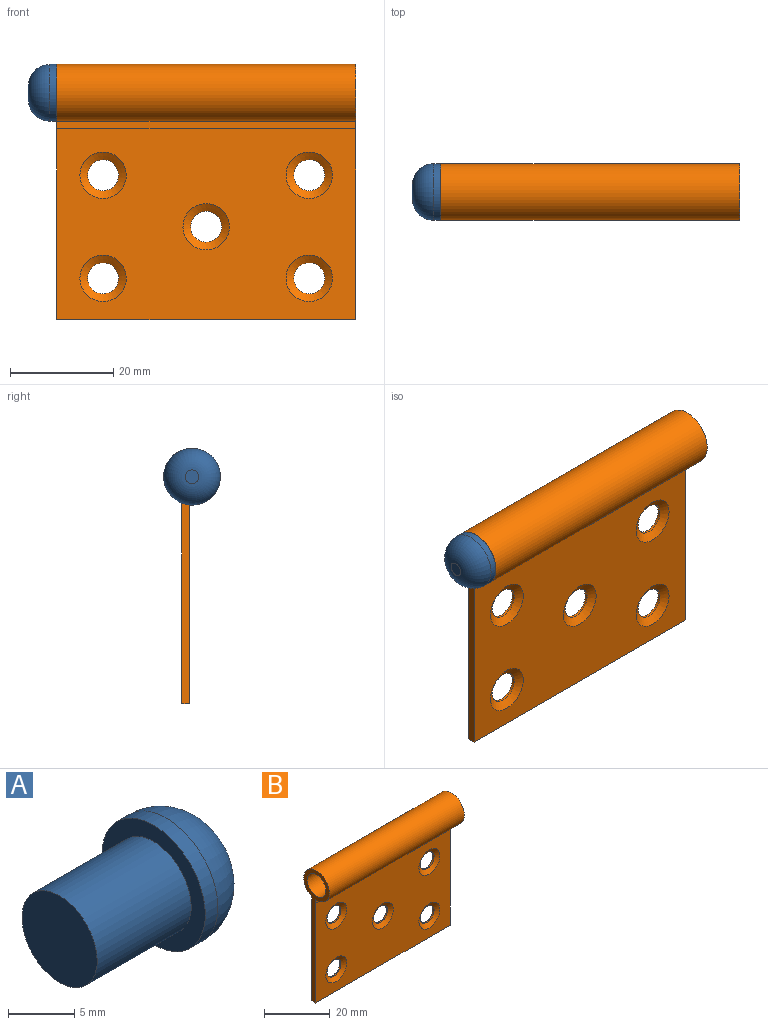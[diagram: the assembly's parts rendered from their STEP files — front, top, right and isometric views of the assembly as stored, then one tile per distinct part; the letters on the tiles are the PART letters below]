
ASSEMBLY  parts=2 mates=1
PART A: 6 faces, bbox 15.5x11x11 mm
  f0: cylinder r=5.5mm len=11mm, axis (-1,0,0), area 46.1mm2, adj f2,f5
  f1: plane 2.67x2.67mm, normal (1,0,0), area 5.6mm2, adj f5
  f2: plane 11x11mm, normal (-1,0,0), area 44.8mm2, adj f0,f3
  f3: cylinder r=4mm len=10mm, axis (1,0,0), area 251.3mm2, adj f2,f4
  f4: plane 8x8mm, normal (-1,0,0), area 50.3mm2, adj f3
  f5: torus R=1.33mm, axis (1,0,0), area 163.9mm2, adj f0,f1
PART B: 19 faces, bbox 58x11x49.5 mm
  f0: extruded ~58x1.52mm, area 88.3mm2, adj f1,f5,f7,f8
  f1: plane 58x37mm, normal (0,-1,0), area 1827.9mm2, adj f0,f2,f7,f8,f14,f15,f16,f17
  f2: plane 58x1.5mm, normal (0,0,-1), area 87mm2, adj f1,f3,f7,f8
  f3: plane 58x37mm, normal (0,1,0), area 2004.6mm2, adj f2,f4,f7,f8,f9,f10,f11,f12
  f4: extruded ~58x1.87mm, area 108.4mm2, adj f3,f5,f7,f8
  f5: cylinder r=5.5mm len=58mm, axis (-1,0,0), area 1915.4mm2, adj f0,f4,f7,f8
  f6: cylinder r=4mm len=58mm, axis (-1,0,0), area 1457.7mm2, adj f7,f8
  f7: plane 49.5x11mm, normal (1,0,0), area 102.8mm2, adj f0,f1,f2,f3,f4,f5,f6
  f8: plane 49.5x11mm, normal (-1,0,0), area 102.8mm2, adj f0,f1,f2,f3,f4,f5,f6
  f9: cylinder r=3mm len=6mm, axis (0,-1,0), area 9.4mm2, adj f3,f17
  f10: cylinder r=3mm len=6mm, axis (0,-1,0), area 9.4mm2, adj f3,f16
  f11: cylinder r=3mm len=6mm, axis (0,-1,0), area 9.4mm2, adj f3,f14
  f12: cylinder r=3mm len=6mm, axis (0,-1,0), area 9.4mm2, adj f3,f18
  f13: cylinder r=3mm len=6mm, axis (0,-1,0), area 9.4mm2, adj f3,f15
  f14: cone r=3mm half-angle=56.3deg, axis (0,-1,0), area 42.5mm2, adj f1,f11
  f15: cone r=3mm half-angle=56.3deg, axis (0,-1,0), area 42.5mm2, adj f1,f13
  f16: cone r=3mm half-angle=56.3deg, axis (0,-1,0), area 42.5mm2, adj f1,f10
  f17: cone r=3mm half-angle=56.3deg, axis (0,-1,0), area 42.5mm2, adj f1,f9
  f18: cone r=3mm half-angle=56.3deg, axis (0,-1,0), area 42.5mm2, adj f1,f12
PLACE A rot(axis=(0,0,1),180deg) t=(-29,-4,0)mm
PLACE B at identity fixed
MATE fastened A.f0 <-> B.f5  axis (-1,0,0) through (-29,-2,184)mm
